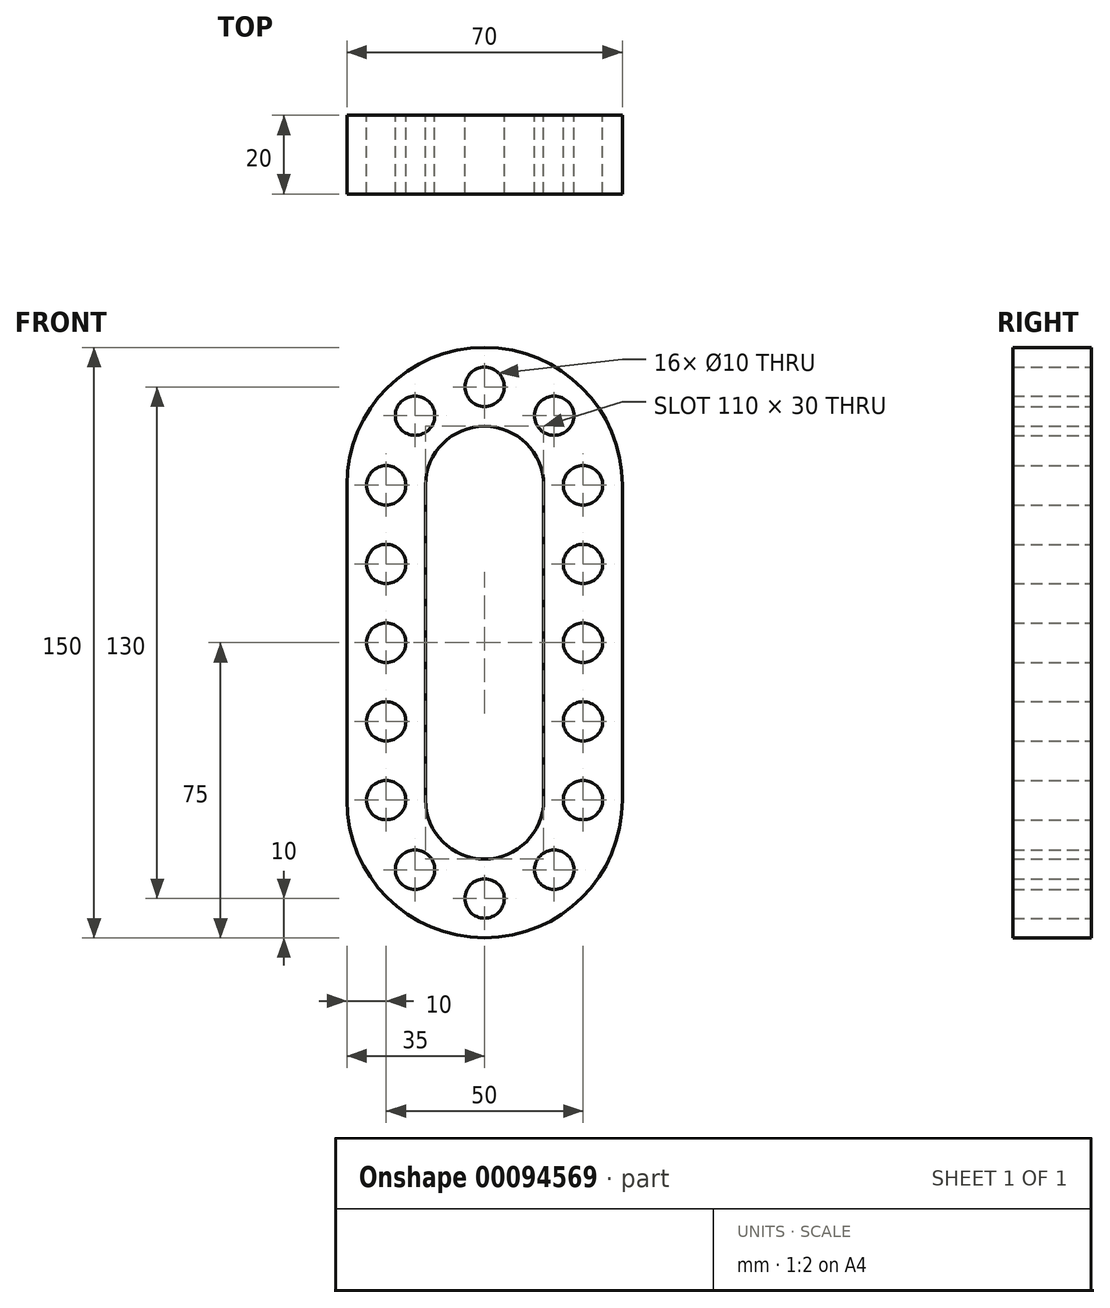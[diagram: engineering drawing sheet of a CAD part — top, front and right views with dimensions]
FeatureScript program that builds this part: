
annotation { "Feature Type Name" : "Feature", "Feature Type Description" : "" }
export const myFeature = defineFeature(function(context is Context, id is Id, definition is map)
    precondition{}
    {
        {
            var Q0;
            Q0=qCreatedBy(makeId("Front.planeOp"),FACE);
            var sketch = newSketch(context, id + "F0", { "sketchPlane" : qUnion([Q0])});
            skPoint(sketch, "E0", {"position": v(-25, 40) * mm});
            skLineSegment(sketch, "E1", {"start": v(-25, 40) * mm, "end": v(-25, 0) * mm, "construction": true});
            skArc(sketch, "E2", {"start": v(0, 65) * mm, "mid": v(-17.68, 57.68) * mm, "end": v(-25, 40) * mm, "construction": true});
            skArc(sketch, "E3.0.startCap", {"start": v(0, 75) * mm, "mid": v(10, 65) * mm, "end": v(0, 55) * mm, "construction": true});
            skArc(sketch, "E3.0.endCap", {"start": v(-15, 40) * mm, "mid": v(-25, 30) * mm, "end": v(-35, 40) * mm, "construction": true});
            skArc(sketch, "E3.0.left", {"start": v(0, 55) * mm, "mid": v(-10.6, 50.6) * mm, "end": v(-15, 40) * mm});
            skArc(sketch, "E3.0.right", {"start": v(0, 75) * mm, "mid": v(-24.75, 64.75) * mm, "end": v(-35, 40) * mm});
            skArc(sketch, "E4.0.startCap", {"start": v(-35, 40) * mm, "mid": v(-25, 50) * mm, "end": v(-15, 40) * mm, "construction": true});
            skArc(sketch, "E4.0.endCap", {"start": v(-15, 0) * mm, "mid": v(-25, -10) * mm, "end": v(-35, 0) * mm, "construction": true});
            skLineSegment(sketch, "E4.0.left", {"start": v(-15, 40) * mm, "end": v(-15, 0) * mm});
            skLineSegment(sketch, "E4.0.right", {"start": v(-35, 40) * mm, "end": v(-35, 0) * mm});
            skCircle(sketch, "E5", {"center": v(-25, 40) * mm, "radius": 5 * mm});
            skCircle(sketch, "E6", {"center": v(-25, 20) * mm, "radius": 5 * mm});
            skCircle(sketch, "E7", {"center": v(-25, 0) * mm, "radius": 5 * mm});
            skPoint(sketch, "E8.center", {"position": v(0, 0) * mm});
            skCircle(sketch, "E9", {"center": v(0, 65) * mm, "radius": 5 * mm});
            skCircle(sketch, "E10", {"center": v(-17.68, 57.68) * mm, "radius": 5 * mm});
            skLineSegment(sketch, "E11.anchor1", {"start": v(0, 40) * mm, "end": v(-25, 40) * mm, "construction": true});
            skLineSegment(sketch, "E11.anchor2", {"start": v(0, 40) * mm, "end": v(0, 65) * mm, "construction": true});
            skLineSegment(sketch, "E12", {"start": v(-35, 0) * mm, "end": v(-30, 0) * mm});
            skLineSegment(sketch, "E13", {"start": v(-25, 0) * mm, "end": v(-15, 0) * mm});
            skLineSegment(sketch, "E14", {"start": v(0, 75) * mm, "end": v(0, 65) * mm});
            skLineSegment(sketch, "E15", {"start": v(0, 65) * mm, "end": v(0, 55) * mm});
            skSolve(sketch);
        }
        {
            var Q0;
            {var subQ4=sQuery(id+"F0.wireOp",EDGE,"E3.0.left");Q0=makeQuery(id+"F0.imprint","IMPRINT",FACE,{"disambiguationData":[TD([[makeQuery(id+"F0.imprint","IMPRINT",EDGE,{"derivedFrom":subQ4}),-1.0]])]});}
            extrude(context, id + "F1", {"entities" : qUnion([Q0]), "depth" : 20 * mm});
        }
        {
            var Q0;
            Q0=makeQuery(id+"F1.opExtrude","SWEPT_BODY",BODY,{"disambiguationData":[OSD([sQuery(id+"F0.wireOp",EDGE,"E3.0.left"),sQuery(id+"F0.wireOp",EDGE,"E3.0.right"),sQuery(id+"F0.wireOp",EDGE,"E4.0.left"),sQuery(id+"F0.wireOp",EDGE,"E4.0.right"),sQuery(id+"F0.wireOp",EDGE,"E5"),sQuery(id+"F0.wireOp",EDGE,"E6"),sQuery(id+"F0.wireOp",EDGE,"E7"),sQuery(id+"F0.wireOp",EDGE,"E9"),sQuery(id+"F0.wireOp",EDGE,"E10"),sQuery(id+"F0.wireOp",EDGE,"E12"),sQuery(id+"F0.wireOp",EDGE,"E13"),sQuery(id+"F0.wireOp",EDGE,"E14"),sQuery(id+"F0.wireOp",EDGE,"E15")])]});
            var Q1;
            Q1=qCreatedBy(makeId("Right.planeOp"),FACE);
            mirror(context, id + "F2", {"operationType" : NewBodyOperationType.ADD, "entities" : qUnion([Q0]), "mirrorPlane" : qUnion([Q1])});
        }
        {
            var Q0;
            Q0=makeQuery(id+"F1.opExtrude","SWEPT_BODY",BODY,{"disambiguationData":[OSD([sQuery(id+"F0.wireOp",EDGE,"E3.0.left"),sQuery(id+"F0.wireOp",EDGE,"E3.0.right"),sQuery(id+"F0.wireOp",EDGE,"E4.0.left"),sQuery(id+"F0.wireOp",EDGE,"E4.0.right"),sQuery(id+"F0.wireOp",EDGE,"E5"),sQuery(id+"F0.wireOp",EDGE,"E6"),sQuery(id+"F0.wireOp",EDGE,"E7"),sQuery(id+"F0.wireOp",EDGE,"E9"),sQuery(id+"F0.wireOp",EDGE,"E10"),sQuery(id+"F0.wireOp",EDGE,"E12"),sQuery(id+"F0.wireOp",EDGE,"E13"),sQuery(id+"F0.wireOp",EDGE,"E14"),sQuery(id+"F0.wireOp",EDGE,"E15")])]});
            var Q1;
            Q1=qCreatedBy(makeId("Top.planeOp"),FACE);
            mirror(context, id + "F3", {"operationType" : NewBodyOperationType.ADD, "entities" : qUnion([Q0]), "mirrorPlane" : qUnion([Q1])});
        }
    });
